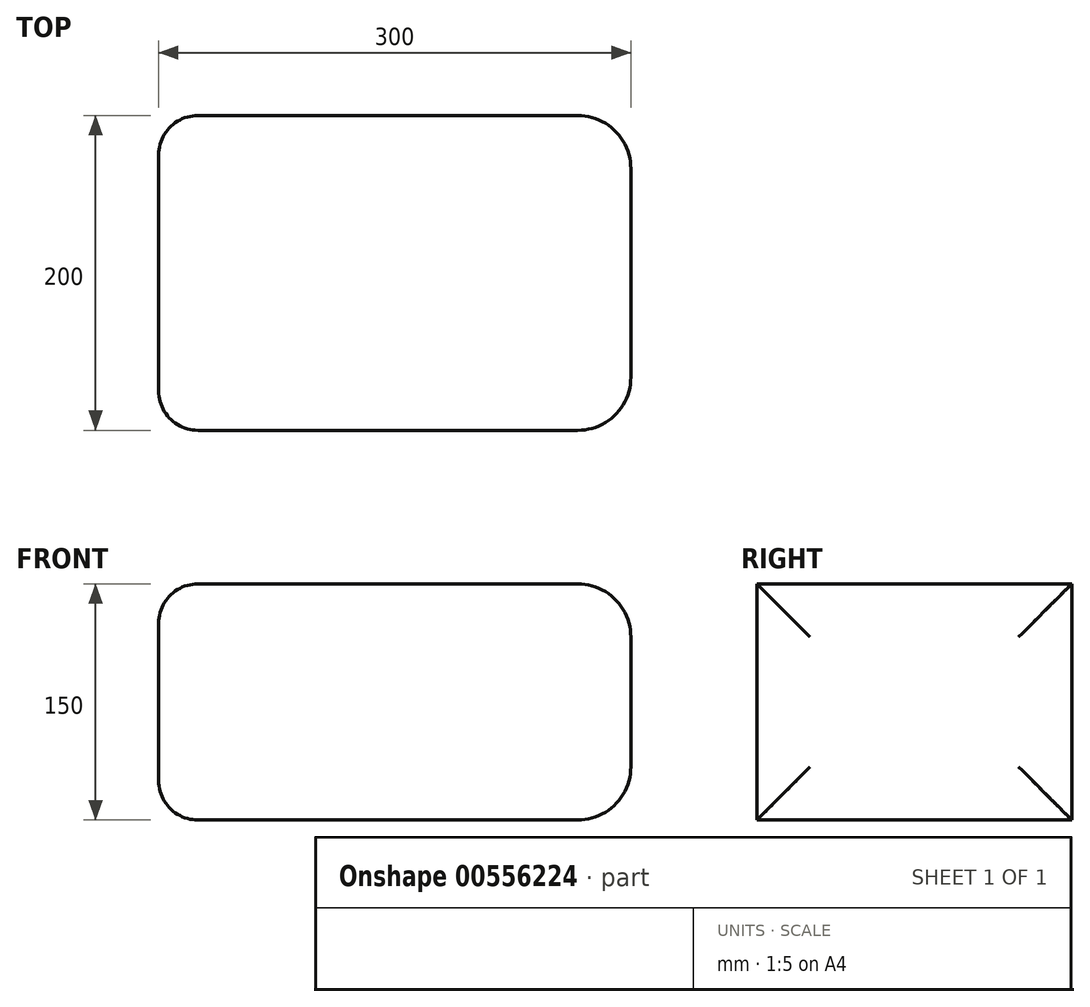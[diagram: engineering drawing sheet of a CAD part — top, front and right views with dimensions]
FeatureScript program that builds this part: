
annotation { "Feature Type Name" : "Feature", "Feature Type Description" : "" }
export const myFeature = defineFeature(function(context is Context, id is Id, definition is map)
    precondition{}
    {
        {
            var Q0;
            Q0=qCreatedBy(makeId("Front.planeOp"),FACE);
            var sketch = newSketch(context, id + "F0", { "sketchPlane" : qUnion([Q0])});
            skLineSegment(sketch, "E0.bottom", {"start": v(0, 0) * mm, "end": v(300, 0) * mm});
            skLineSegment(sketch, "E0.top", {"start": v(0, 150) * mm, "end": v(300, 150) * mm});
            skLineSegment(sketch, "E0.left", {"start": v(0, 0) * mm, "end": v(0, 150) * mm});
            skLineSegment(sketch, "E0.right", {"start": v(300, 0) * mm, "end": v(300, 150) * mm});
            skSolve(sketch);
        }
        {
            var Q0;
            Q0=makeQuery(id+"F0.imprint","IMPRINT",FACE,{"disambiguationData":[TD([[makeQuery(id+"F0.imprint","IMPRINT",EDGE,{"derivedFrom":sQuery(id+"F0.wireOp",EDGE,"E0.bottom")}),1.0]])]});
            extrude(context, id + "F1", {"entities" : qUnion([Q0]), "depth" : 200 * mm, "offsetDistance" : 25 * mm});
        }
        {
            var Q0;
            Q0=makeQuery(id+"F1.opExtrude","CAP_FACE",FACE,{"disambiguationData":[OSD([sQuery(id+"F0.wireOp",EDGE,"E0.bottom"),sQuery(id+"F0.wireOp",EDGE,"E0.top"),sQuery(id+"F0.wireOp",EDGE,"E0.left"),sQuery(id+"F0.wireOp",EDGE,"E0.right")])],"isStart":false});
            var sketch = newSketch(context, id + "F2", { "sketchPlane" : qUnion([Q0])});
            skSolve(sketch);
        }
        {
            var Q0;
            Q0=makeQuery(id+"F1.opExtrude","SWEPT_EDGE",EDGE,{"disambiguationData":[OSD([sQuery(id+"F0.wireOp",EDGE,"E0.top"),sQuery(id+"F0.wireOp",EDGE,"E0.right")])]});
            var Q1;
            Q1=makeQuery(id+"F1.opExtrude","SWEPT_FACE",FACE,{"disambiguationData":[OSD([sQuery(id+"F0.wireOp",EDGE,"E0.right")])]});
            fillet(context, id + "F3", {"entities" : qUnion([Q0, Q1]), "radius" : 33.8 * mm, "tangentPropagation" : true, "allowEdgeOverflow" : false});
        }
        {
            var Q0;
            Q0=makeQuery(id+"F1.opExtrude","SWEPT_FACE",FACE,{"disambiguationData":[OSD([sQuery(id+"F0.wireOp",EDGE,"E0.left")])]});
            fillet(context, id + "F4", {"entities" : qUnion([Q0]), "radius" : 25 * mm, "tangentPropagation" : true, "allowEdgeOverflow" : false});
        }
    });
